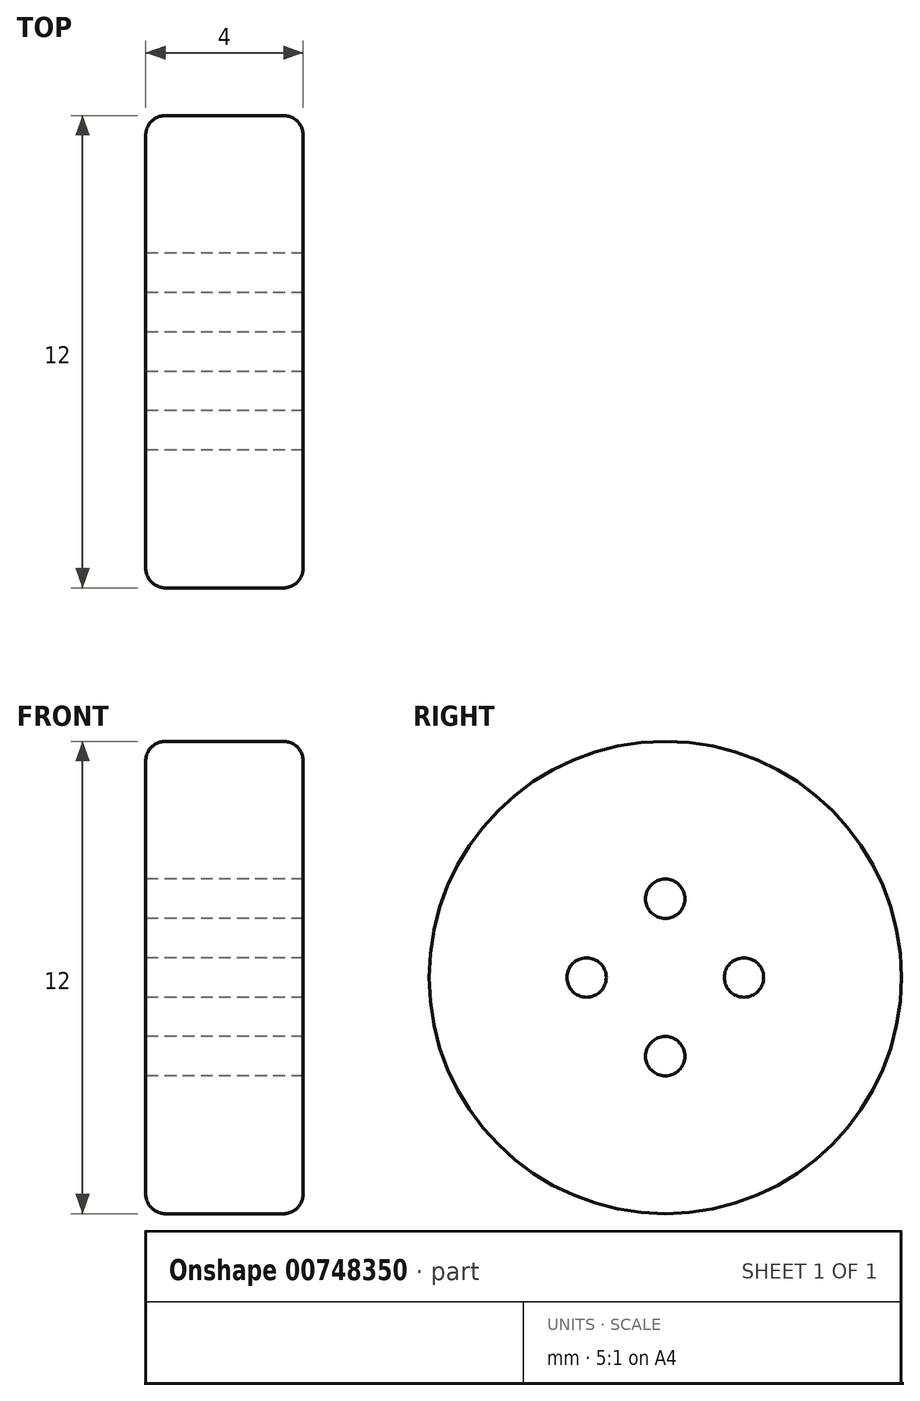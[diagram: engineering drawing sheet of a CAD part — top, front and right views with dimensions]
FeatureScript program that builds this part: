
annotation { "Feature Type Name" : "Feature", "Feature Type Description" : "" }
export const myFeature = defineFeature(function(context is Context, id is Id, definition is map)
    precondition{}
    {
        {
            var Q0;
            Q0=qCreatedBy(makeId("Right.planeOp"),FACE);
            var sketch = newSketch(context, id + "F0", { "sketchPlane" : qUnion([Q0])});
            skCircle(sketch, "E0", {"center": v(0, 0) * mm, "radius": 6 * mm});
            skCircle(sketch, "E1", {"center": v(0, 2) * mm, "radius": 0.5 * mm});
            skCircle(sketch, "E2.1.0", {"center": v(-2, 0) * mm, "radius": 0.5 * mm});
            skCircle(sketch, "E2.2.0", {"center": v(0, -2) * mm, "radius": 0.5 * mm});
            skCircle(sketch, "E2.3.0", {"center": v(2, 0) * mm, "radius": 0.5 * mm});
            skSolve(sketch);
        }
        {
            var Q0;
            Q0 = qSketchRegion(id + "F0", true);
            extrude(context, id + "F1", {"entities" : qUnion([Q0]), "depth" : 4 * mm, "offsetDistance" : 25 * mm});
        }
        {
            var Q0;
            Q0=makeQuery(id+"F1.opExtrude","CAP_EDGE",EDGE,{"disambiguationData":[OSD([sQuery(id+"F0.wireOp",EDGE,"E0")])],"isStart":false});
            var Q1;
            Q1=makeQuery(id+"F1.opExtrude","CAP_EDGE",EDGE,{"disambiguationData":[OSD([sQuery(id+"F0.wireOp",EDGE,"E0")])],"isStart":true});
            fillet(context, id + "F2", {"entities" : qUnion([Q0, Q1]), "radius" : .5 * mm, "tangentPropagation" : true, "allowEdgeOverflow" : false});
        }
    });
